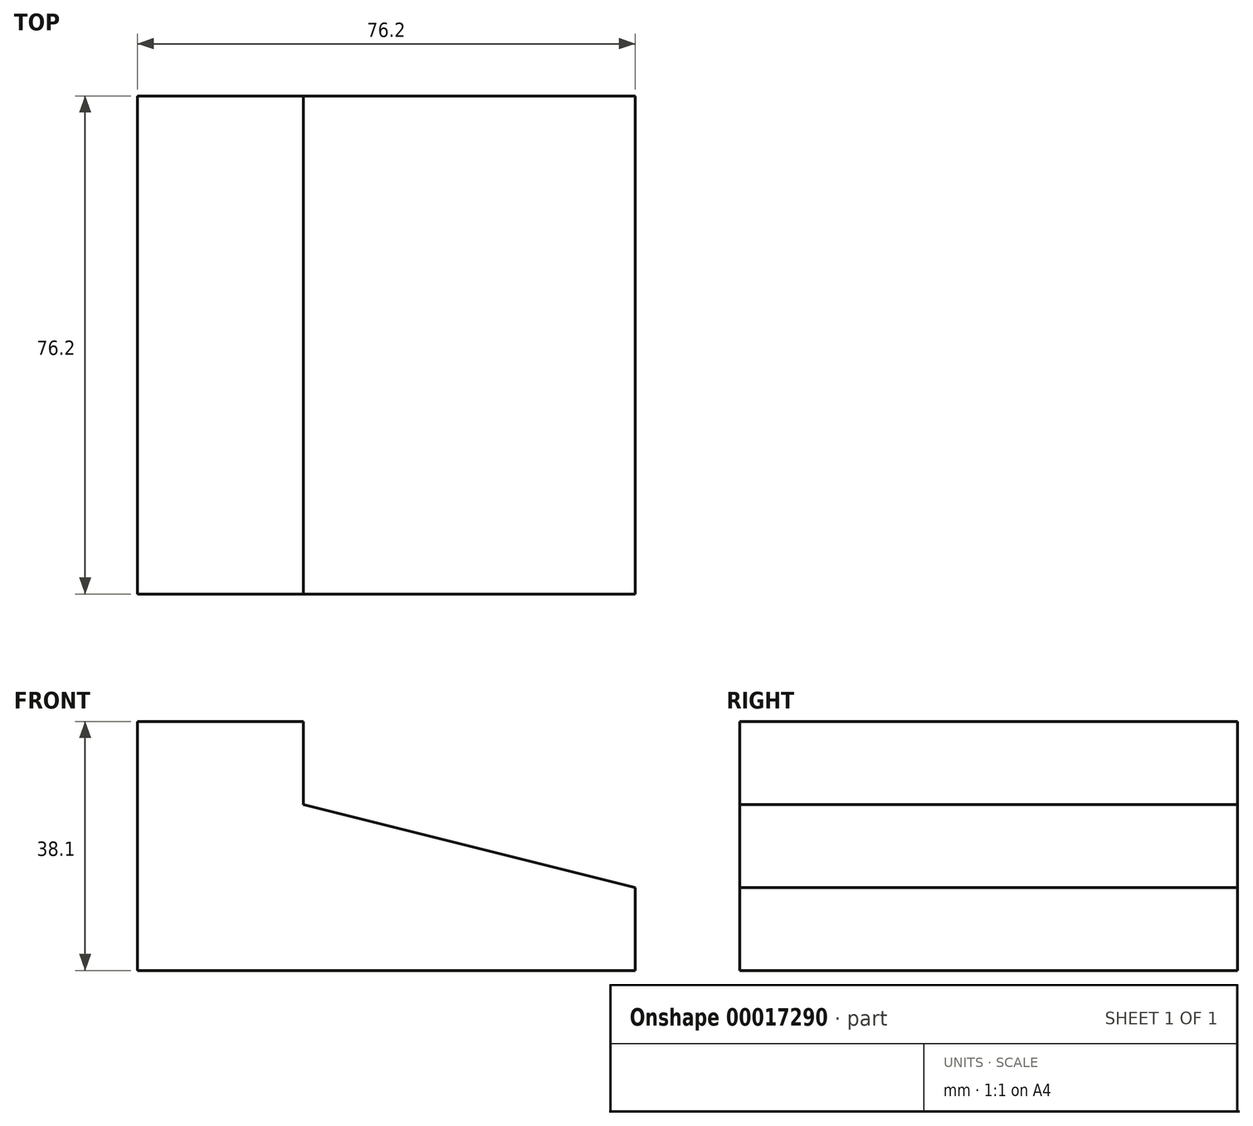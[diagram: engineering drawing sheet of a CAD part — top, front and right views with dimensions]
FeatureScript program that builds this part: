
annotation { "Feature Type Name" : "Feature", "Feature Type Description" : "" }
export const myFeature = defineFeature(function(context is Context, id is Id, definition is map)
    precondition{}
    {
        {
            var Q0;
            Q0=qCreatedBy(makeId("Front.planeOp"),FACE);
            var sketch = newSketch(context, id + "F0", { "sketchPlane" : qUnion([Q0])});
            skLineSegment(sketch, "E0", {"start": v(-6.98, 26.13) * mm, "end": v(-6.98, -11.97) * mm});
            skLineSegment(sketch, "E1", {"start": v(-6.98, -11.97) * mm, "end": v(69.22, -11.97) * mm});
            skLineSegment(sketch, "E2", {"start": v(69.22, -11.97) * mm, "end": v(69.22, 0.73) * mm});
            skLineSegment(sketch, "E3", {"start": v(69.22, 0.73) * mm, "end": v(18.42, 13.43) * mm});
            skLineSegment(sketch, "E4", {"start": v(18.42, 13.43) * mm, "end": v(18.42, 26.13) * mm});
            skLineSegment(sketch, "E5", {"start": v(-6.98, 26.13) * mm, "end": v(18.42, 26.13) * mm});
            skSolve(sketch);
        }
        {
            var Q0;
            Q0=makeQuery(id+"F0.imprint","IMPRINT",FACE,{"disambiguationData":[TD([[makeQuery(id+"F0.imprint","IMPRINT",EDGE,{"derivedFrom":sQuery(id+"F0.wireOp",EDGE,"E0")}),1.0]])]});
            extrude(context, id + "F1", {"entities" : qUnion([Q0]), "depth" : 76.2 * mm});
        }
    });
